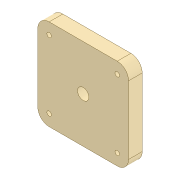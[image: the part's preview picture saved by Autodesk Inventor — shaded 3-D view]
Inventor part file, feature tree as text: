
AUTODESK INVENTOR PART (.ipt)
format: ipt  version: 2020 (Build 240168000, 168)  size: 107,520 bytes
history: native  units: mm
features: other x5, extrude x1
ambient origin geometry x8: Origin, YZ Plane, XZ Plane, XY Plane, X Axis, Y Axis, Z Axis, Center Point
bodies: Body1 (feature_tree)
feature tree (6):
  other  "Sólido1"
  other  "Plano de trabalho1"
  extrude  "Extrusão1"  Depth=10.0mm
  other  "<userpath>\OneDrive\Área de Trabalho\Calorimetro 2022\Inventor\parte_superior.iam"
  other  "parte_superior.iam"
  other  "Corpo_1:4"
